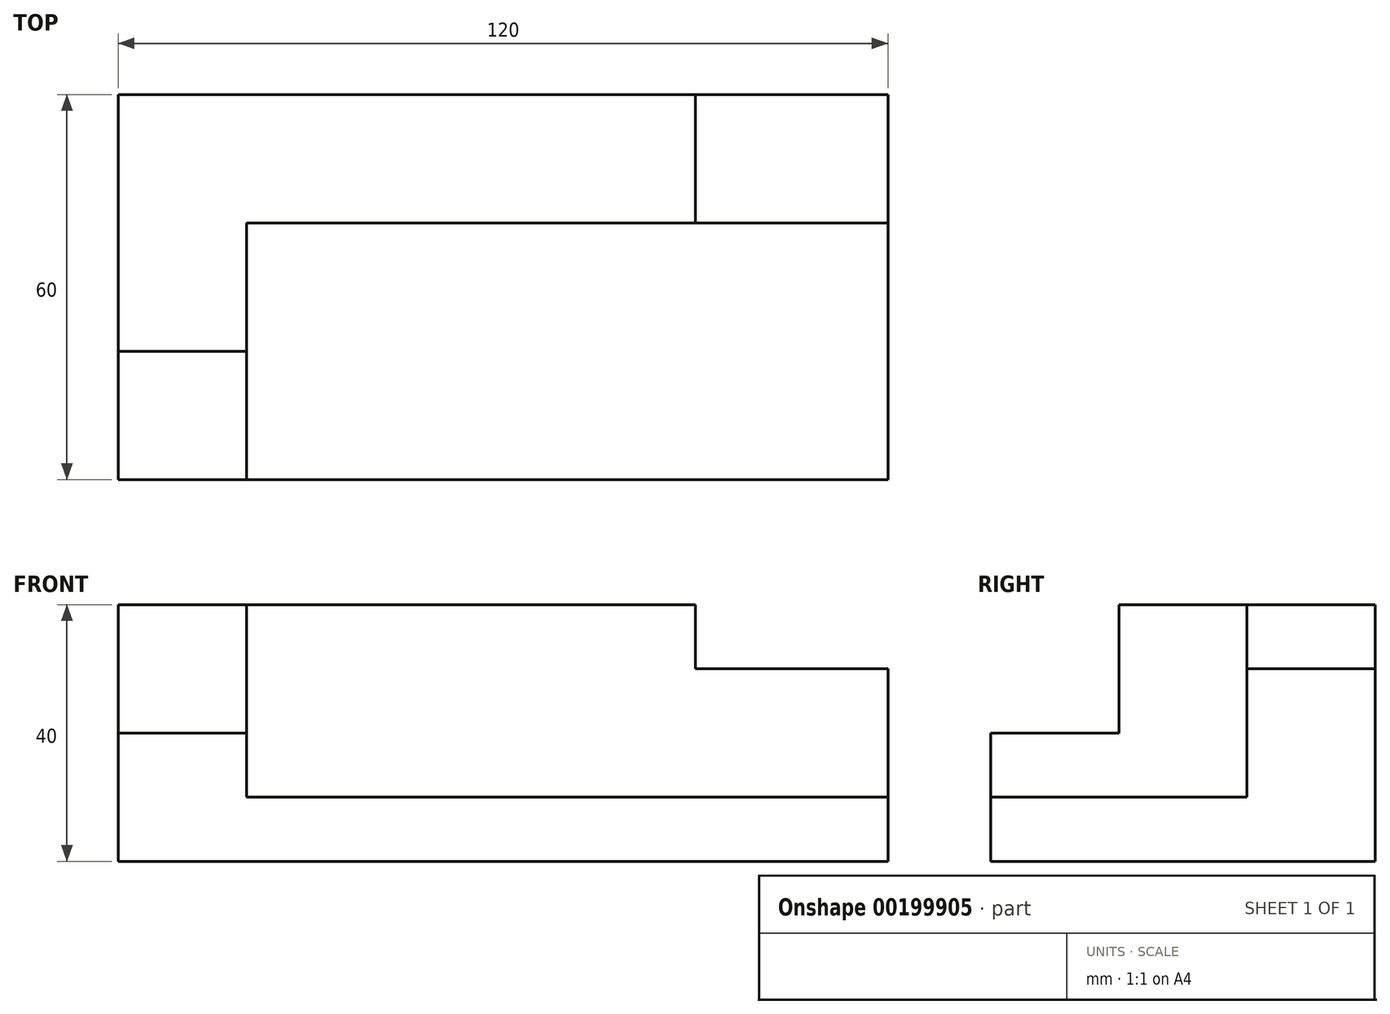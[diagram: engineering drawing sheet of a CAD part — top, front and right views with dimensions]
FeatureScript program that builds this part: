
annotation { "Feature Type Name" : "Feature", "Feature Type Description" : "" }
export const myFeature = defineFeature(function(context is Context, id is Id, definition is map)
    precondition{}
    {
        {
            var Q0;
            Q0=qCreatedBy(makeId("Front.planeOp"),FACE);
            var sketch = newSketch(context, id + "F0", { "sketchPlane" : qUnion([Q0])});
            skLineSegment(sketch, "E0", {"start": v(0, 0) * mm, "end": v(-120, 0) * mm});
            skLineSegment(sketch, "E1", {"start": v(-120, 0) * mm, "end": v(-120, 40) * mm});
            skLineSegment(sketch, "E2", {"start": v(-30, 40) * mm, "end": v(-120, 40) * mm});
            skLineSegment(sketch, "E3", {"start": v(-30, 40) * mm, "end": v(-30, 30) * mm});
            skLineSegment(sketch, "E4", {"start": v(-30, 30) * mm, "end": v(0, 30) * mm});
            skLineSegment(sketch, "E5", {"start": v(0, 30) * mm, "end": v(0, 0) * mm});
            skLineSegment(sketch, "E6", {"start": v(-120, 20) * mm, "end": v(-100, 20) * mm});
            skLineSegment(sketch, "E7", {"start": v(-100, 20) * mm, "end": v(-100, 40) * mm});
            skLineSegment(sketch, "E8", {"start": v(-100, 10) * mm, "end": v(0, 10) * mm});
            skLineSegment(sketch, "E9", {"start": v(-100, 10) * mm, "end": v(-100, 20) * mm});
            skSolve(sketch);
        }
        {
            var Q0;
            {var subQ3=sQuery(id+"F0.wireOp",EDGE,"E6");Q0=makeQuery(id+"F0.imprint","IMPRINT",FACE,{"disambiguationData":[TD([[makeQuery(id+"F0.imprint","IMPRINT",EDGE,{"derivedFrom":subQ3}),1.0]])]});}
            extrude(context, id + "F1", {"entities" : qUnion([Q0]), "depth" : 40 * mm});
        }
        {
            var Q0;
            {var subQ2=sQuery(id+"F0.wireOp",EDGE,"E0");Q0=makeQuery(id+"F0.imprint","IMPRINT",FACE,{"disambiguationData":[TD([[makeQuery(id+"F0.imprint","IMPRINT",EDGE,{"derivedFrom":subQ2}),-1.0]])]});}
            extrude(context, id + "F2", {"entities" : qUnion([Q0]), "operationType" : NewBodyOperationType.ADD, "depth" : 60 * mm});
        }
        {
            var Q0;
            {var subQ3=sQuery(id+"F0.wireOp",EDGE,"E3");Q0=makeQuery(id+"F0.imprint","IMPRINT",FACE,{"disambiguationData":[TD([[makeQuery(id+"F0.imprint","IMPRINT",EDGE,{"derivedFrom":subQ3}),-1.0]])]});}
            extrude(context, id + "F3", {"entities" : qUnion([Q0]), "operationType" : NewBodyOperationType.ADD, "depth" : 20 * mm});
        }
    });
